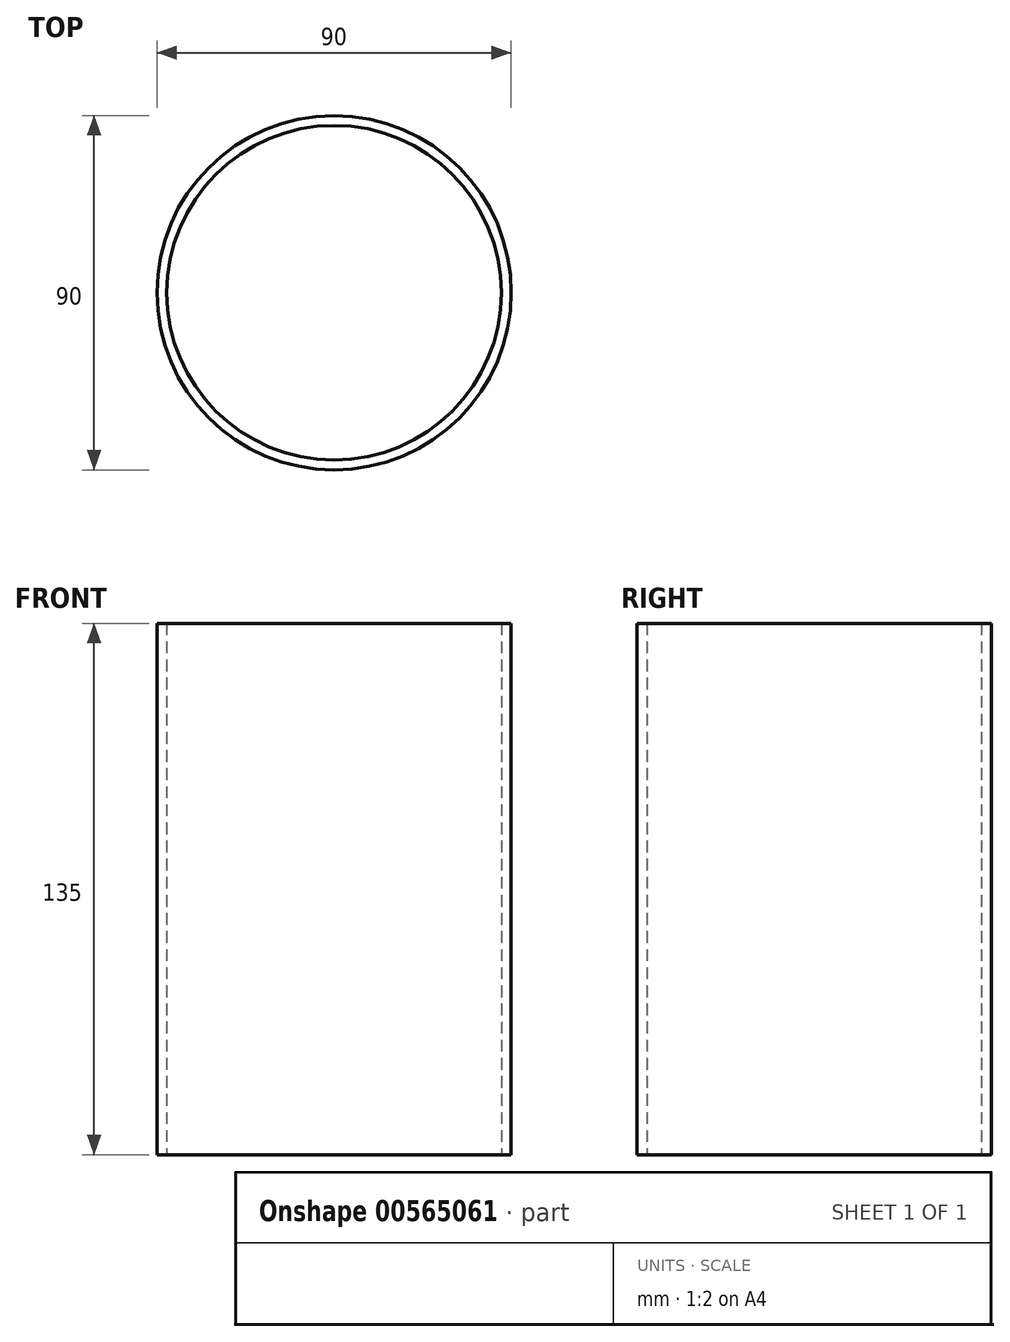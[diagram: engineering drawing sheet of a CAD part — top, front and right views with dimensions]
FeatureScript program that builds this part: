
annotation { "Feature Type Name" : "Feature", "Feature Type Description" : "" }
export const myFeature = defineFeature(function(context is Context, id is Id, definition is map)
    precondition{}
    {
        {
            var Q0;
            Q0=qCreatedBy(makeId("Top.planeOp"),FACE);
            var sketch = newSketch(context, id + "F0", { "sketchPlane" : qUnion([Q0])});
            skCircle(sketch, "E0", {"center": v(0, 0) * mm, "radius": 42.5 * mm});
            skCircle(sketch, "E1", {"center": v(0, 0) * mm, "radius": 45 * mm});
            skSolve(sketch);
        }
        {
            var Q0;
            Q0 = qSketchRegion(id + "F0", true);
            extrude(context, id + "F1", {"entities" : qUnion([Q0]), "depth" : 135 * mm, "offsetDistance" : 25 * mm});
        }
    });
